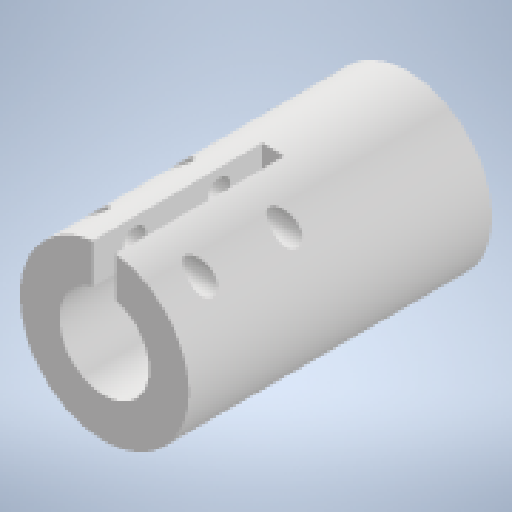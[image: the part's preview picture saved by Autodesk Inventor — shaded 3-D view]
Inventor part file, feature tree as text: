
AUTODESK INVENTOR PART (.ipt)
format: ipt  version: 2023 (Build 270158000, 158)  size: 220,672 bytes
history: native  units: mm
features: other x4, extrude x3, sketch x3, projected_geometry x3, reference x1
ambient origin geometry x8: Origin, YZ Plane, XZ Plane, XY Plane, X Axis, Y Axis, Z Axis, Center Point
bodies: Solid1 (feature_tree)
feature tree (14):
  extrude  "Extrusion1"  Depth=12.0mm TaperAngle=0.0deg
  extrude  "Extrusion2"  Depth=2.0mm
  extrude  "Extrusion3"  Depth=15.0mm TaperAngle=0.0deg
  sketch  "Sketch1"  dims[d0=15.0mm d1=12.0mm d2=0.0mm]
  reference  "Reference1"
  sketch  "Sketch2"  dims[d3=8.0mm d4=2.0mm]
  projected_geometry  "Projected Loop1"
  sketch  "Sketch3"  dims[d5=15.0mm d6=15.0mm d7=0.0mm d8=2.0mm d9=2.0mm d10=15.0mm d11=0.0mm]
  projected_geometry  "Projected Loop2"
  projected_geometry  "Projected Loop3"
  other  "<userpath>\OneDrive\Namizje\school\4. letnik\Matura\Izdelovanje\3D model\3D_skenner.iam"
  other  "3D_skenner.iam"
  other  "Spur Gears1_CPY:1"
  other  "Spur Gear11_CPY:1"
